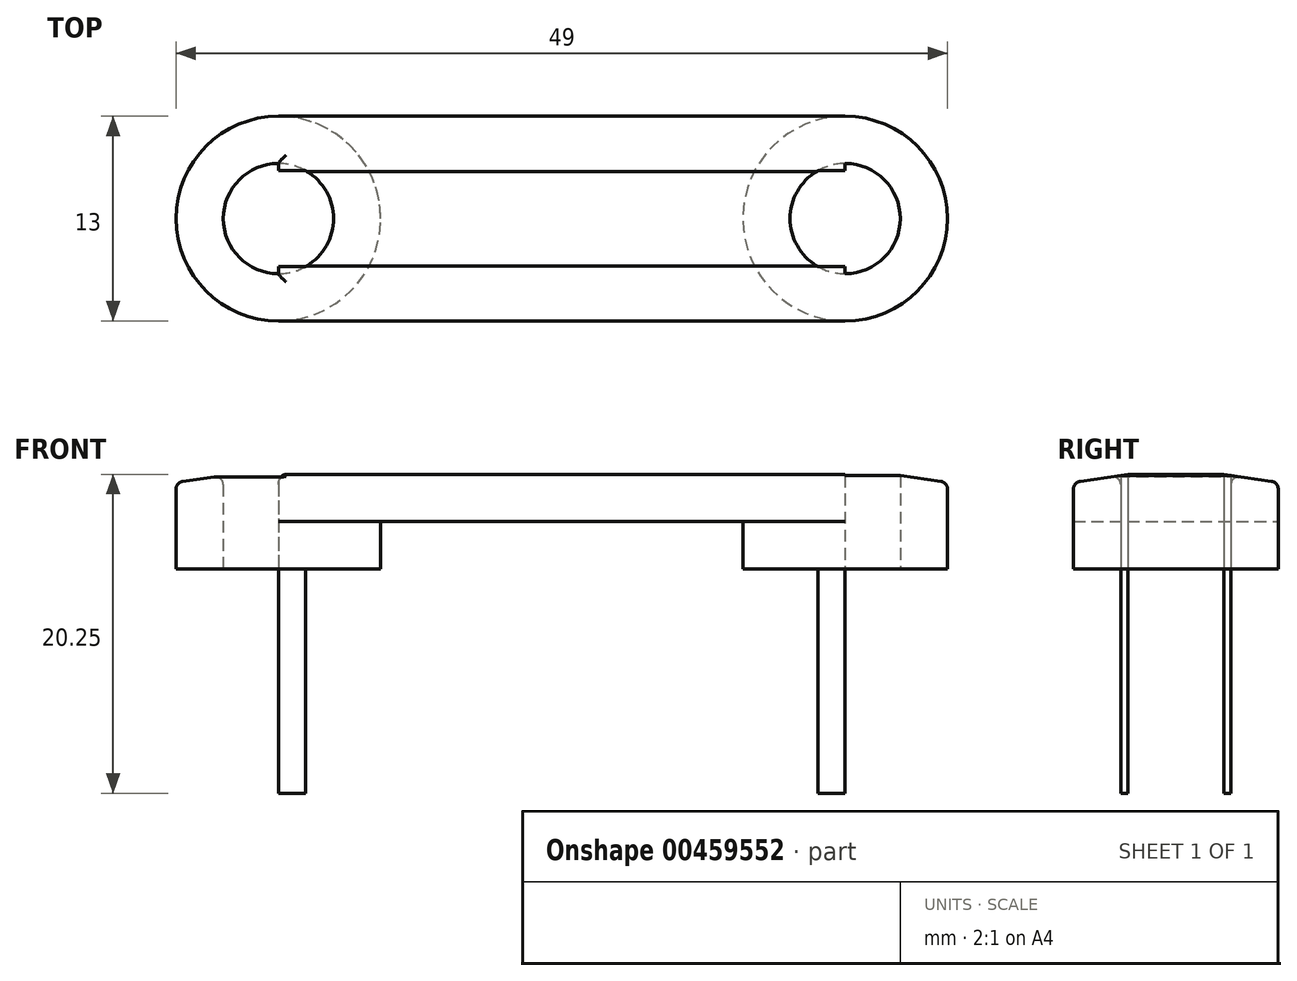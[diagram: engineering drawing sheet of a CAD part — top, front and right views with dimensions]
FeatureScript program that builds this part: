
annotation { "Feature Type Name" : "Feature", "Feature Type Description" : "" }
export const myFeature = defineFeature(function(context is Context, id is Id, definition is map)
    precondition{}
    {
        {
            var Q0;
            Q0=qCreatedBy(makeId("Top.planeOp"),FACE);
            var sketch = newSketch(context, id + "F0", { "sketchPlane" : qUnion([Q0])});
            skLineSegment(sketch, "E0.bottom", {"start": v(18, 6.5) * mm, "end": v(-18, 6.5) * mm});
            skLineSegment(sketch, "E0.top", {"start": v(18, -6.5) * mm, "end": v(-18, -6.5) * mm});
            skPoint(sketch, "E0.middle", {"position": v(0, 0) * mm});
            skCircle(sketch, "E1", {"center": v(-18, 0) * mm, "radius": 6.5 * mm});
            skCircle(sketch, "E2", {"center": v(18, 0) * mm, "radius": 6.5 * mm});
            skCircle(sketch, "E3", {"center": v(-18, 0) * mm, "radius": 3.5 * mm});
            skCircle(sketch, "E4", {"center": v(18, 0) * mm, "radius": 3.5 * mm});
            skLineSegment(sketch, "E5.bottom", {"start": v(-18, 3.5) * mm, "end": v(18, 3.5) * mm});
            skLineSegment(sketch, "E5.top", {"start": v(-18, -3.5) * mm, "end": v(18, -3.5) * mm});
            skLineSegment(sketch, "E5.left", {"start": v(-18, 3.5) * mm, "end": v(-18, -3.5) * mm});
            skLineSegment(sketch, "E5.right", {"start": v(18, 3.5) * mm, "end": v(18, -3.5) * mm});
            skLineSegment(sketch, "E6.bottom", {"start": v(18, 3.05) * mm, "end": v(-18, 3.05) * mm});
            skLineSegment(sketch, "E6.top", {"start": v(18, -3.05) * mm, "end": v(-18, -3.05) * mm});
            skLineSegment(sketch, "E6.left", {"start": v(18, 3.05) * mm, "end": v(18, -3.05) * mm});
            skLineSegment(sketch, "E6.right", {"start": v(-18, 3.05) * mm, "end": v(-18, -3.05) * mm});
            skSolve(sketch);
        }
        {
            var Q0;
            Q0=makeQuery(id+"F0.imprint","IMPRINT",FACE,{"disambiguationData":[TD([[makeQuery(id+"F0.imprint","IMPRINT",EDGE,{"derivedFrom":sQuery(id+"F0.wireOp",EDGE,"E4")}),-1.0]])]});
            var Q1;
            Q1=makeQuery(id+"F0.imprint","IMPRINT",FACE,{"disambiguationData":[TD([[makeQuery(id+"F0.imprint","IMPRINT",EDGE,{"derivedFrom":sQuery(id+"F0.wireOp",EDGE,"E3")}),1.0]])]});
            var Q2;
            {var subQ0=sQuery(id+"F0.wireOp",EDGE,"E0.bottom");Q2=makeQuery(id+"F0.imprint","IMPRINT",FACE,{"disambiguationData":[TD([[makeQuery(id+"F0.imprint","IMPRINT",EDGE,{"derivedFrom":subQ0}),1.0]])]});}
            var Q3;
            Q3=makeQuery(id+"F0.imprint","IMPRINT",FACE,{"disambiguationData":[TD([[makeQuery(id+"F0.imprint","IMPRINT",EDGE,{"derivedFrom":sQuery(id+"F0.wireOp",EDGE,"E3")}),-1.0]])]});
            var Q4;
            Q4=makeQuery(id+"F0.imprint","IMPRINT",FACE,{"disambiguationData":[TD([[makeQuery(id+"F0.imprint","IMPRINT",EDGE,{"derivedFrom":sQuery(id+"F0.wireOp",EDGE,"E4")}),1.0]])]});
            var Q5;
            Q5=makeQuery(id+"F0.imprint","IMPRINT",FACE,{"disambiguationData":[TD([[makeQuery(id+"F0.imprint","IMPRINT",EDGE,{"derivedFrom":sQuery(id+"F0.wireOp",EDGE,"ayjcYqf9-YWka-kVYJ-lzEs-o3r7Y0wh9yZo")}),1.0]])]});
            var Q6;
            Q6=makeQuery(id+"F0.imprint","IMPRINT",FACE,{"disambiguationData":[TD([[makeQuery(id+"F0.imprint","IMPRINT",EDGE,{"derivedFrom":sQuery(id+"F0.wireOp",EDGE,"fbrzEOdP-8T9M-SPR5-fSJk-swAH3sFxK75i")}),1.0]])]});
            var Q7;
            {var subQ6=sQuery(id+"F0.wireOp",EDGE,"E1");var subQ9=makeQuery(id+"F0.imprint","INTERSECT",VERTEX,{"derivedFrom":[sQuery(id+"F0.wireOp",EDGE,"E0.bottom"),subQ6]});Q7=makeQuery(id+"F0.imprint","IMPRINT",FACE,{"disambiguationData":[TD([[makeQuery(id+"F0.imprint","IMPRINT",EDGE,{"disambiguationData":[TD([[subQ9,1.0]])],"derivedFrom":subQ6}),1.0]])]});}
            var Q8;
            {var subQ0=sQuery(id+"F0.wireOp",EDGE,"E5.bottom");var subQ1=sQuery(id+"F0.wireOp",EDGE,"E1");var subQ2=makeQuery(id+"F0.imprint","INTERSECT",VERTEX,{"derivedFrom":[subQ1,subQ0]});Q8=makeQuery(id+"F0.imprint","IMPRINT",FACE,{"disambiguationData":[TD([[makeQuery(id+"F0.imprint","IMPRINT",EDGE,{"disambiguationData":[TD([[subQ2,1.0]])],"derivedFrom":subQ1}),-1.0]])]});}
            var Q9;
            {var subQ0=sQuery(id+"F0.wireOp",EDGE,"E0.top");Q9=makeQuery(id+"F0.imprint","IMPRINT",FACE,{"disambiguationData":[TD([[makeQuery(id+"F0.imprint","IMPRINT",EDGE,{"derivedFrom":subQ0}),-1.0]])]});}
            var Q10;
            {var subQ0=sQuery(id+"F0.wireOp",EDGE,"E2");var subQ1=makeQuery(id+"F0.imprint","INTERSECT",VERTEX,{"derivedFrom":[sQuery(id+"F0.wireOp",EDGE,"E0.bottom"),subQ0]});Q10=makeQuery(id+"F0.imprint","IMPRINT",FACE,{"disambiguationData":[TD([[makeQuery(id+"F0.imprint","IMPRINT",EDGE,{"disambiguationData":[TD([[subQ1,-1.0]])],"derivedFrom":subQ0}),1.0]])]});}
            var Q11;
            {var subQ5=sQuery(id+"F0.wireOp",EDGE,"E6.right");Q11=makeQuery(id+"F0.imprint","IMPRINT",FACE,{"disambiguationData":[TD([[makeQuery(id+"F0.imprint","IMPRINT",EDGE,{"derivedFrom":subQ5}),1.0]])]});}
            var Q12;
            {var subQ4=sQuery(id+"F0.wireOp",EDGE,"E6.right");Q12=makeQuery(id+"F0.imprint","IMPRINT",FACE,{"disambiguationData":[TD([[makeQuery(id+"F0.imprint","IMPRINT",EDGE,{"derivedFrom":subQ4}),-1.0]])]});}
            var Q13;
            {var subQ0=sQuery(id+"F0.wireOp",EDGE,"E6.bottom");var subQ1=sQuery(id+"F0.wireOp",EDGE,"E1");var subQ2=makeQuery(id+"F0.imprint","INTERSECT",VERTEX,{"derivedFrom":[subQ1,subQ0]});Q13=makeQuery(id+"F0.imprint","IMPRINT",FACE,{"disambiguationData":[TD([[makeQuery(id+"F0.imprint","IMPRINT",EDGE,{"disambiguationData":[TD([[subQ2,1.0]])],"derivedFrom":subQ1}),-1.0]])]});}
            var Q14;
            {var subQ5=sQuery(id+"F0.wireOp",EDGE,"E6.left");Q14=makeQuery(id+"F0.imprint","IMPRINT",FACE,{"disambiguationData":[TD([[makeQuery(id+"F0.imprint","IMPRINT",EDGE,{"derivedFrom":subQ5}),-1.0]])]});}
            var Q15;
            {var subQ4=sQuery(id+"F0.wireOp",EDGE,"E6.left");Q15=makeQuery(id+"F0.imprint","IMPRINT",FACE,{"disambiguationData":[TD([[makeQuery(id+"F0.imprint","IMPRINT",EDGE,{"derivedFrom":subQ4}),1.0]])]});}
            var Q16;
            {var subQ0=sQuery(id+"F0.wireOp",EDGE,"E5.top");var subQ1=sQuery(id+"F0.wireOp",EDGE,"E1");var subQ2=makeQuery(id+"F0.imprint","INTERSECT",VERTEX,{"derivedFrom":[subQ1,subQ0]});Q16=makeQuery(id+"F0.imprint","IMPRINT",FACE,{"disambiguationData":[TD([[makeQuery(id+"F0.imprint","IMPRINT",EDGE,{"disambiguationData":[TD([[subQ2,-1.0]])],"derivedFrom":subQ1}),-1.0]])]});}
            extrude(context, id + "F1", {"entities" : qUnion([Q0, Q1, Q2, Q3, Q4, Q5, Q6, Q7, Q8, Q9, Q10, Q11, Q12, Q13, Q14, Q15, Q16]), "depth" : 3 * mm});
        }
        {
            var Q0;
            Q0=makeQuery(id+"F0.imprint","IMPRINT",FACE,{"disambiguationData":[TD([[makeQuery(id+"F0.imprint","IMPRINT",EDGE,{"derivedFrom":sQuery(id+"F0.wireOp",EDGE,"E3")}),-1.0]])]});
            var Q1;
            Q1=makeQuery(id+"F0.imprint","IMPRINT",FACE,{"disambiguationData":[TD([[makeQuery(id+"F0.imprint","IMPRINT",EDGE,{"derivedFrom":sQuery(id+"F0.wireOp",EDGE,"E4")}),-1.0]])]});
            var Q2;
            {var subQ0=sQuery(id+"F0.wireOp",EDGE,"E2");var subQ1=makeQuery(id+"F0.imprint","INTERSECT",VERTEX,{"derivedFrom":[sQuery(id+"F0.wireOp",EDGE,"E0.bottom"),subQ0]});Q2=makeQuery(id+"F0.imprint","IMPRINT",FACE,{"disambiguationData":[TD([[makeQuery(id+"F0.imprint","IMPRINT",EDGE,{"disambiguationData":[TD([[subQ1,-1.0]])],"derivedFrom":subQ0}),1.0]])]});}
            var Q3;
            {var subQ6=sQuery(id+"F0.wireOp",EDGE,"E1");var subQ9=makeQuery(id+"F0.imprint","INTERSECT",VERTEX,{"derivedFrom":[sQuery(id+"F0.wireOp",EDGE,"E0.bottom"),subQ6]});Q3=makeQuery(id+"F0.imprint","IMPRINT",FACE,{"disambiguationData":[TD([[makeQuery(id+"F0.imprint","IMPRINT",EDGE,{"disambiguationData":[TD([[subQ9,1.0]])],"derivedFrom":subQ6}),1.0]])]});}
            extrude(context, id + "F2", {"entities" : qUnion([Q0, Q1, Q2, Q3]), "operationType" : NewBodyOperationType.ADD, "oppositeDirection" : true, "depth" : 3 * mm});
        }
        {
            var Q0;
            Q0=makeQuery(id+"F0.imprint","IMPRINT",FACE,{"disambiguationData":[TD([[makeQuery(id+"F0.imprint","IMPRINT",EDGE,{"derivedFrom":sQuery(id+"F0.wireOp",EDGE,"E3")}),1.0]])]});
            var Q1;
            Q1=makeQuery(id+"F0.imprint","IMPRINT",FACE,{"disambiguationData":[TD([[makeQuery(id+"F0.imprint","IMPRINT",EDGE,{"derivedFrom":sQuery(id+"F0.wireOp",EDGE,"fbrzEOdP-8T9M-SPR5-fSJk-swAH3sFxK75i")}),1.0]])]});
            var Q2;
            Q2=makeQuery(id+"F0.imprint","IMPRINT",FACE,{"disambiguationData":[TD([[makeQuery(id+"F0.imprint","IMPRINT",EDGE,{"derivedFrom":sQuery(id+"F0.wireOp",EDGE,"E4")}),1.0]])]});
            var Q3;
            Q3=makeQuery(id+"F0.imprint","IMPRINT",FACE,{"disambiguationData":[TD([[makeQuery(id+"F0.imprint","IMPRINT",EDGE,{"derivedFrom":sQuery(id+"F0.wireOp",EDGE,"ayjcYqf9-YWka-kVYJ-lzEs-o3r7Y0wh9yZo")}),1.0]])]});
            var Q4;
            {var subQ4=sQuery(id+"F0.wireOp",EDGE,"E6.left");Q4=makeQuery(id+"F0.imprint","IMPRINT",FACE,{"disambiguationData":[TD([[makeQuery(id+"F0.imprint","IMPRINT",EDGE,{"derivedFrom":subQ4}),1.0]])]});}
            var Q5;
            {var subQ5=sQuery(id+"F0.wireOp",EDGE,"E6.left");Q5=makeQuery(id+"F0.imprint","IMPRINT",FACE,{"disambiguationData":[TD([[makeQuery(id+"F0.imprint","IMPRINT",EDGE,{"derivedFrom":subQ5}),-1.0]])]});}
            var Q6;
            {var subQ5=sQuery(id+"F0.wireOp",EDGE,"E6.right");Q6=makeQuery(id+"F0.imprint","IMPRINT",FACE,{"disambiguationData":[TD([[makeQuery(id+"F0.imprint","IMPRINT",EDGE,{"derivedFrom":subQ5}),1.0]])]});}
            var Q7;
            {var subQ4=sQuery(id+"F0.wireOp",EDGE,"E6.right");Q7=makeQuery(id+"F0.imprint","IMPRINT",FACE,{"disambiguationData":[TD([[makeQuery(id+"F0.imprint","IMPRINT",EDGE,{"derivedFrom":subQ4}),-1.0]])]});}
            extrude(context, id + "F3", {"entities" : qUnion([Q0, Q1, Q2, Q3, Q4, Q5, Q6, Q7]), "operationType" : NewBodyOperationType.ADD, "oppositeDirection" : true, "depth" : 17.25 * mm});
        }
        {
            var Q0;
            Q0=qCreatedBy(makeId("Front.planeOp"),FACE);
            var sketch = newSketch(context, id + "F4", { "sketchPlane" : qUnion([Q0])});
            skLineSegment(sketch, "E7.bottom", {"start": v(0, 0) * mm, "end": v(-21.5, 0) * mm});
            skLineSegment(sketch, "E7.top", {"start": v(0, -3) * mm, "end": v(-21.5, -3) * mm});
            skLineSegment(sketch, "E7.left", {"start": v(0, 0) * mm, "end": v(0, -3) * mm});
            skLineSegment(sketch, "E7.right", {"start": v(-21.5, 0) * mm, "end": v(-21.5, -3) * mm});
            skLineSegment(sketch, "E8", {"start": v(-21.5, -3) * mm, "end": v(-21.5, -4.5) * mm});
            skLineSegment(sketch, "E9.bottom", {"start": v(0, 0) * mm, "end": v(21.5, 0) * mm});
            skLineSegment(sketch, "E9.top", {"start": v(0, -3) * mm, "end": v(21.5, -3) * mm});
            skLineSegment(sketch, "E9.right", {"start": v(21.5, 0) * mm, "end": v(21.5, -3) * mm});
            skLineSegment(sketch, "E10", {"start": v(21.5, -3) * mm, "end": v(21.5, -4.5) * mm});
            skArc(sketch, "E11", {"start": v(-21.5, -4.5) * mm, "mid": v(-20.75, -3.75) * mm, "end": v(-21.5, -3) * mm});
            skArc(sketch, "E12", {"start": v(21.5, -3) * mm, "mid": v(20.75, -3.75) * mm, "end": v(21.5, -4.5) * mm});
            skSolve(sketch);
        }
        {
            var Q0;
            Q0=makeQuery(id+"F4.imprint","IMPRINT",FACE,{"disambiguationData":[TD([[makeQuery(id+"F4.imprint","IMPRINT",EDGE,{"derivedFrom":sQuery(id+"F4.wireOp",EDGE,"E8")}),1.0]])]});
            var Q1;
            Q1=makeQuery(id+"F4.imprint","IMPRINT",FACE,{"disambiguationData":[TD([[makeQuery(id+"F4.imprint","IMPRINT",EDGE,{"derivedFrom":sQuery(id+"F4.wireOp",EDGE,"E10")}),-1.0]])]});
            extrude(context, id + "F5", {"entities" : qUnion([Q0, Q1]), "operationType" : NewBodyOperationType.REMOVE, "oppositeDirection" : true, "depth" : 25 * mm});
        }
        {
            var Q0;
            Q0=makeQuery(id+"F4.imprint","IMPRINT",FACE,{"disambiguationData":[TD([[makeQuery(id+"F4.imprint","IMPRINT",EDGE,{"derivedFrom":sQuery(id+"F4.wireOp",EDGE,"E8")}),1.0]])]});
            var Q1;
            Q1=makeQuery(id+"F4.imprint","IMPRINT",FACE,{"disambiguationData":[TD([[makeQuery(id+"F4.imprint","IMPRINT",EDGE,{"derivedFrom":sQuery(id+"F4.wireOp",EDGE,"E10")}),-1.0]])]});
            extrude(context, id + "F6", {"entities" : qUnion([Q0, Q1]), "operationType" : NewBodyOperationType.REMOVE, "depth" : 25 * mm});
        }
        {
            var Q0;
            Q0=makeQuery(id+"F1.opExtrude","CAP_EDGE",EDGE,{"disambiguationData":[OSD([sQuery(id+"F0.wireOp",EDGE,"E0.top")])],"isStart":false});
            var Q1;
            Q1=makeQuery(id+"F1.opExtrude","CAP_EDGE",EDGE,{"disambiguationData":[OSD([sQuery(id+"F0.wireOp",EDGE,"E2")])],"isStart":false});
            var Q2;
            Q2=makeQuery(id+"F1.opExtrude","CAP_EDGE",EDGE,{"disambiguationData":[OSD([sQuery(id+"F0.wireOp",EDGE,"E1")])],"isStart":false});
            var Q3;
            Q3=makeQuery(id+"F1.opExtrude","CAP_EDGE",EDGE,{"disambiguationData":[OSD([sQuery(id+"F0.wireOp",EDGE,"E0.bottom")])],"isStart":false});
            chamfer(context, id + "F7", {"entities" : qUnion([Q0, Q1, Q2, Q3]), "chamferType" : ChamferType.TWO_OFFSETS, "width1" : 0.5 * mm, "oppositeDirection" : false, "width2" : 3.5 * mm, "tangentPropagation" : true});
        }
        {
            var Q0;
            {var subQ0=sQuery(id+"F0.wireOp",EDGE,"E0.top");Q0=makeQuery(id+"F7.opChamfer","BLEND_EDGE",EDGE,{"blendedFrom":[makeQuery(id+"F1.opExtrude","CAP_EDGE",EDGE,{"disambiguationData":[OSD([subQ0])],"isStart":false}),makeQuery(id+"F1.opExtrude","SWEPT_FACE",FACE,{"disambiguationData":[OSD([subQ0])]})],"blendedInto":[makeQuery(id+"F1.opExtrude","SWEPT_FACE",FACE,{"disambiguationData":[OSD([subQ0])]})]});}
            var Q1;
            Q1=makeQuery(id+"F7.opChamfer","BLEND_FACE",FACE,{"disambiguationData":[OSD([sQuery(id+"F0.wireOp",EDGE,"E1")])]});
            var Q2;
            {var subQ0=sQuery(id+"F0.wireOp",EDGE,"E0.bottom");Q2=makeQuery(id+"F7.opChamfer","BLEND_EDGE",EDGE,{"blendedFrom":[makeQuery(id+"F1.opExtrude","CAP_EDGE",EDGE,{"disambiguationData":[OSD([subQ0])],"isStart":false}),makeQuery(id+"F1.opExtrude","SWEPT_FACE",FACE,{"disambiguationData":[OSD([subQ0])]})],"blendedInto":[makeQuery(id+"F1.opExtrude","SWEPT_FACE",FACE,{"disambiguationData":[OSD([subQ0])]})]});}
            var Q3;
            {var subQ0=sQuery(id+"F0.wireOp",EDGE,"E2");Q3=makeQuery(id+"F7.opChamfer","BLEND_EDGE",EDGE,{"blendedFrom":[makeQuery(id+"F1.opExtrude","CAP_EDGE",EDGE,{"disambiguationData":[OSD([subQ0])],"isStart":false}),makeQuery(id+"F2.boolean.opBoolean","MERGE",FACE,{"derivedFrom":[makeQuery(id+"F1.opExtrude","SWEPT_FACE",FACE,{"disambiguationData":[OSD([subQ0])]}),makeQuery(id+"F2.opExtrude","SWEPT_FACE",FACE,{"disambiguationData":[OSD([subQ0])]})]})],"blendedInto":[makeQuery(id+"F2.boolean.opBoolean","MERGE",FACE,{"derivedFrom":[makeQuery(id+"F1.opExtrude","SWEPT_FACE",FACE,{"disambiguationData":[OSD([subQ0])]}),makeQuery(id+"F2.opExtrude","SWEPT_FACE",FACE,{"disambiguationData":[OSD([subQ0])]})]})]});}
            fillet(context, id + "F8", {"entities" : qUnion([Q0, Q1, Q2, Q3]), "radius" : .5 * mm, "tangentPropagation" : true, "allowEdgeOverflow" : false});
        }
    });
